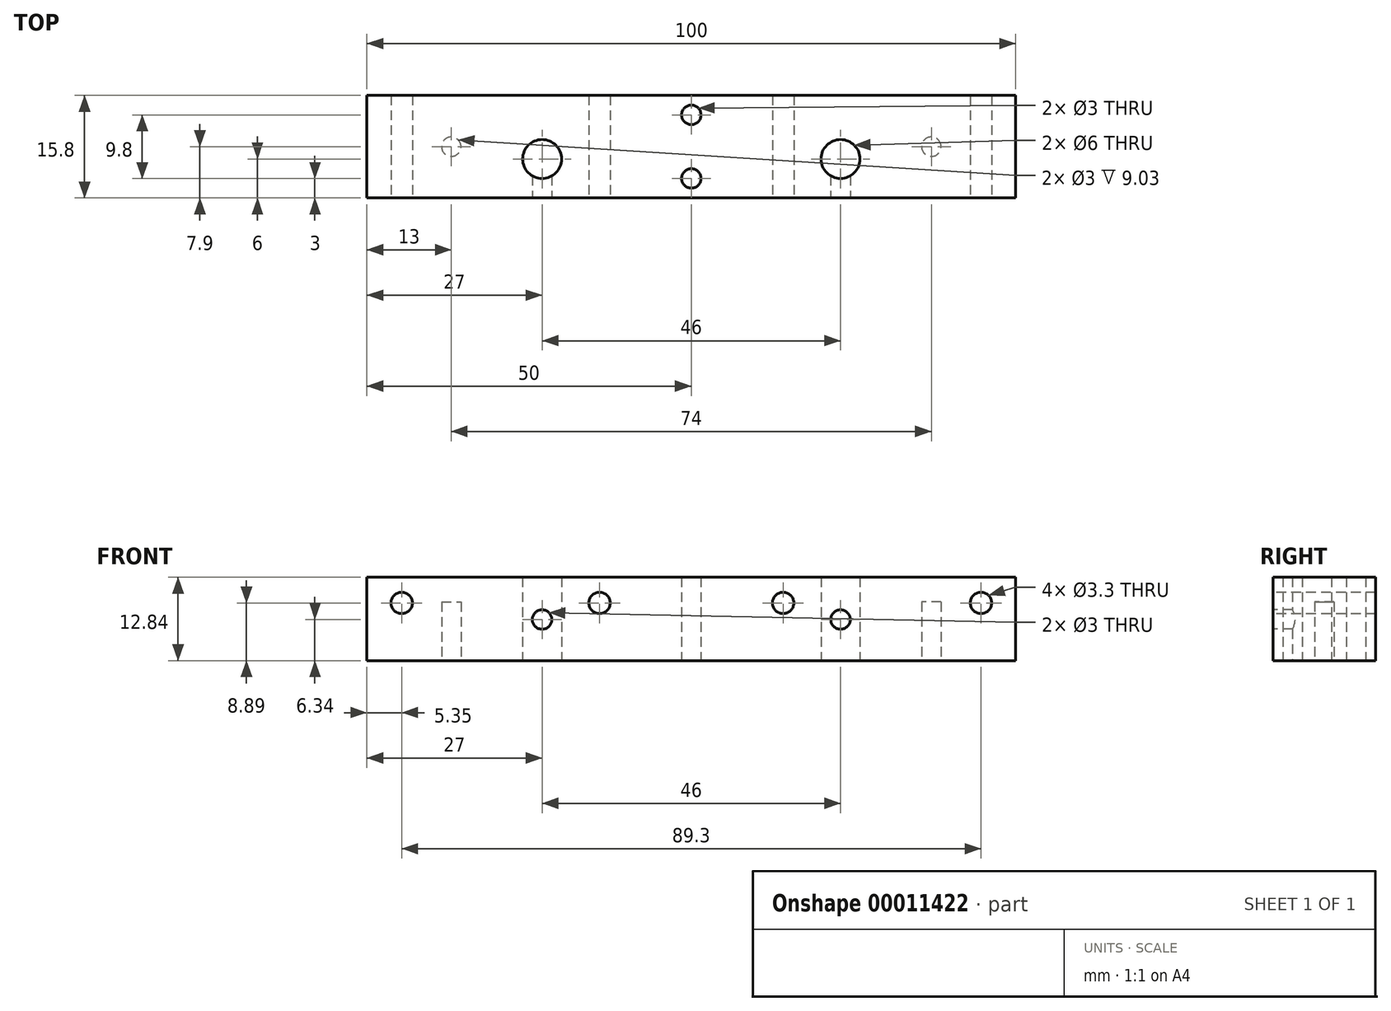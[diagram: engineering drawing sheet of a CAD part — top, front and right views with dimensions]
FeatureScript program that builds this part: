
annotation { "Feature Type Name" : "Feature", "Feature Type Description" : "" }
export const myFeature = defineFeature(function(context is Context, id is Id, definition is map)
    precondition{}
    {
        {
            var Q0;
            Q0=qCreatedBy(makeId("Top.planeOp"),FACE);
            var sketch = newSketch(context, id + "F0", { "sketchPlane" : qUnion([Q0])});
            skLineSegment(sketch, "E0.rect.bottom", {"start": v(-50, 7.9) * mm, "end": v(0, 7.9) * mm});
            skLineSegment(sketch, "E0.rect.top", {"start": v(-50, -7.9) * mm, "end": v(0, -7.9) * mm});
            skLineSegment(sketch, "E0.rect.left", {"start": v(-50, 7.9) * mm, "end": v(-50, -7.9) * mm});
            skPoint(sketch, "E0.rect.middle", {"position": v(0, 0) * mm});
            skLineSegment(sketch, "E1", {"start": v(0, 7.9) * mm, "end": v(0, 6.4) * mm});
            skArc(sketch, "E2", {"start": v(0, -3.4) * mm, "mid": v(-1.5, -4.9) * mm, "end": v(0, -6.4) * mm});
            skArc(sketch, "E3", {"start": v(0, 6.4) * mm, "mid": v(-1.5, 4.9) * mm, "end": v(0, 3.4) * mm});
            skCircle(sketch, "E4.0.MirrorC", {"center": v(-23, -1.9) * mm, "radius": 3 * mm});
            skLineSegment(sketch, "E5.trimOffspring", {"start": v(0, 3.4) * mm, "end": v(0, -3.4) * mm});
            skLineSegment(sketch, "E6.trimOffspring", {"start": v(0, -6.4) * mm, "end": v(0, -7.9) * mm});
            skSolve(sketch);
        }
        {
            var Q0;
            Q0=makeQuery(id+"F0.imprint","IMPRINT",FACE,{"disambiguationData":[TD([[makeQuery(id+"F0.imprint","IMPRINT",EDGE,{"derivedFrom":sQuery(id+"F0.wireOp",EDGE,"E0.rect.bottom")}),-1.0]])]});
            extrude(context, id + "F1", {"entities" : qUnion([Q0]), "depth" : 12.84 * mm});
        }
        {
            var Q0;
            Q0=makeQuery(id+"F1.opExtrude","SWEPT_FACE",FACE,{"disambiguationData":[OSD([sQuery(id+"F0.wireOp",EDGE,"E0.rect.top")])]});
            var sketch = newSketch(context, id + "F2", { "sketchPlane" : qUnion([Q0])});
            skCircle(sketch, "E7", {"center": v(-44.65, 8.9) * mm, "radius": 1.65 * mm});
            skCircle(sketch, "E8", {"center": v(-14.15, 8.9) * mm, "radius": 1.65 * mm});
            skCircle(sketch, "E9", {"center": v(-23, 6.34) * mm, "radius": 1.5 * mm});
            skLineSegment(sketch, "E10.0", {"start": v(-20, 12.84) * mm, "end": v(-26, 12.84) * mm, "construction": true});
            skLineSegment(sketch, "E11", {"start": v(-23, 12.84) * mm, "end": v(-23, 0) * mm, "construction": true});
            skSolve(sketch);
        }
        {
            var Q0;
            Q0=makeQuery(id+"F2.imprint","IMPRINT",FACE,{"disambiguationData":[TD([[makeQuery(id+"F2.imprint","IMPRINT",EDGE,{"derivedFrom":sQuery(id+"F2.wireOp",EDGE,"E7")}),1.0]])]});
            var Q1;
            Q1=makeQuery(id+"F2.imprint","IMPRINT",FACE,{"disambiguationData":[TD([[makeQuery(id+"F2.imprint","IMPRINT",EDGE,{"derivedFrom":sQuery(id+"F2.wireOp",EDGE,"E8")}),1.0]])]});
            var Q2;
            Q2=makeQuery(id+"F2.imprint","IMPRINT",FACE,{"disambiguationData":[TD([[makeQuery(id+"F2.imprint","IMPRINT",EDGE,{"derivedFrom":sQuery(id+"F2.wireOp",EDGE,"E9")}),1.0]])]});
            extrude(context, id + "F3", {"entities" : qUnion([Q0, Q1, Q2]), "operationType" : NewBodyOperationType.REMOVE, "endBound" : BoundingType.UP_TO_NEXT, "oppositeDirection" : true, "depth" : 25 * mm});
        }
        {
            var Q0;
            {var subQ0=makeQuery(id+"F1.opExtrude","CAP_FACE",FACE,{"disambiguationData":[OSD([sQuery(id+"F0.wireOp",EDGE,"E0.rect.bottom"),sQuery(id+"F0.wireOp",EDGE,"E0.rect.top"),sQuery(id+"F0.wireOp",EDGE,"E0.rect.left"),sQuery(id+"F0.wireOp",EDGE,"E1"),sQuery(id+"F0.wireOp",EDGE,"E2"),sQuery(id+"F0.wireOp",EDGE,"E3"),sQuery(id+"F0.wireOp",EDGE,"E4.0.MirrorC"),sQuery(id+"F0.wireOp",EDGE,"E5.trimOffspring"),sQuery(id+"F0.wireOp",EDGE,"E6.trimOffspring")])],"isStart":true});Q0=makeQuery(id+"F6.boolean.opBoolean","MERGE",FACE,{"derivedFrom":[subQ0,makeQuery(id+"F6.opPattern","COPY",FACE,{"derivedFrom":subQ0,"instanceName":"1"})]});}
            var sketch = newSketch(context, id + "F4", { "sketchPlane" : qUnion([Q0])});
            skLineSegment(sketch, "E12", {"start": v(0, 7.9) * mm, "end": v(0, -7.9) * mm, "construction": true});
            skCircle(sketch, "E13", {"center": v(-37, 0) * mm, "radius": 1.5 * mm});
            skSolve(sketch);
        }
        {
            var Q0;
            Q0 = qSketchRegion(id + "F4", true);
            extrude(context, id + "F5", {"entities" : qUnion([Q0]), "operationType" : NewBodyOperationType.REMOVE, "oppositeDirection" : true, "depth" : 9.03 * mm});
        }
        {
            var Q0;
            Q0=makeQuery(id+"F1.opExtrude","SWEPT_BODY",BODY,{"disambiguationData":[OSD([sQuery(id+"F0.wireOp",EDGE,"E0.rect.bottom"),sQuery(id+"F0.wireOp",EDGE,"E0.rect.top"),sQuery(id+"F0.wireOp",EDGE,"E0.rect.left"),sQuery(id+"F0.wireOp",EDGE,"E1"),sQuery(id+"F0.wireOp",EDGE,"E2"),sQuery(id+"F0.wireOp",EDGE,"E3"),sQuery(id+"F0.wireOp",EDGE,"E4.0.MirrorC"),sQuery(id+"F0.wireOp",EDGE,"E5.trimOffspring"),sQuery(id+"F0.wireOp",EDGE,"E6.trimOffspring")])]});
            var Q1;
            Q1=makeQuery(id+"F1.opExtrude","SWEPT_FACE",FACE,{"disambiguationData":[OSD([sQuery(id+"F0.wireOp",EDGE,"E5.trimOffspring")])]});
            mirror(context, id + "F6", {"operationType" : NewBodyOperationType.ADD, "entities" : qUnion([Q0]), "mirrorPlane" : qUnion([Q1])});
        }
    });
